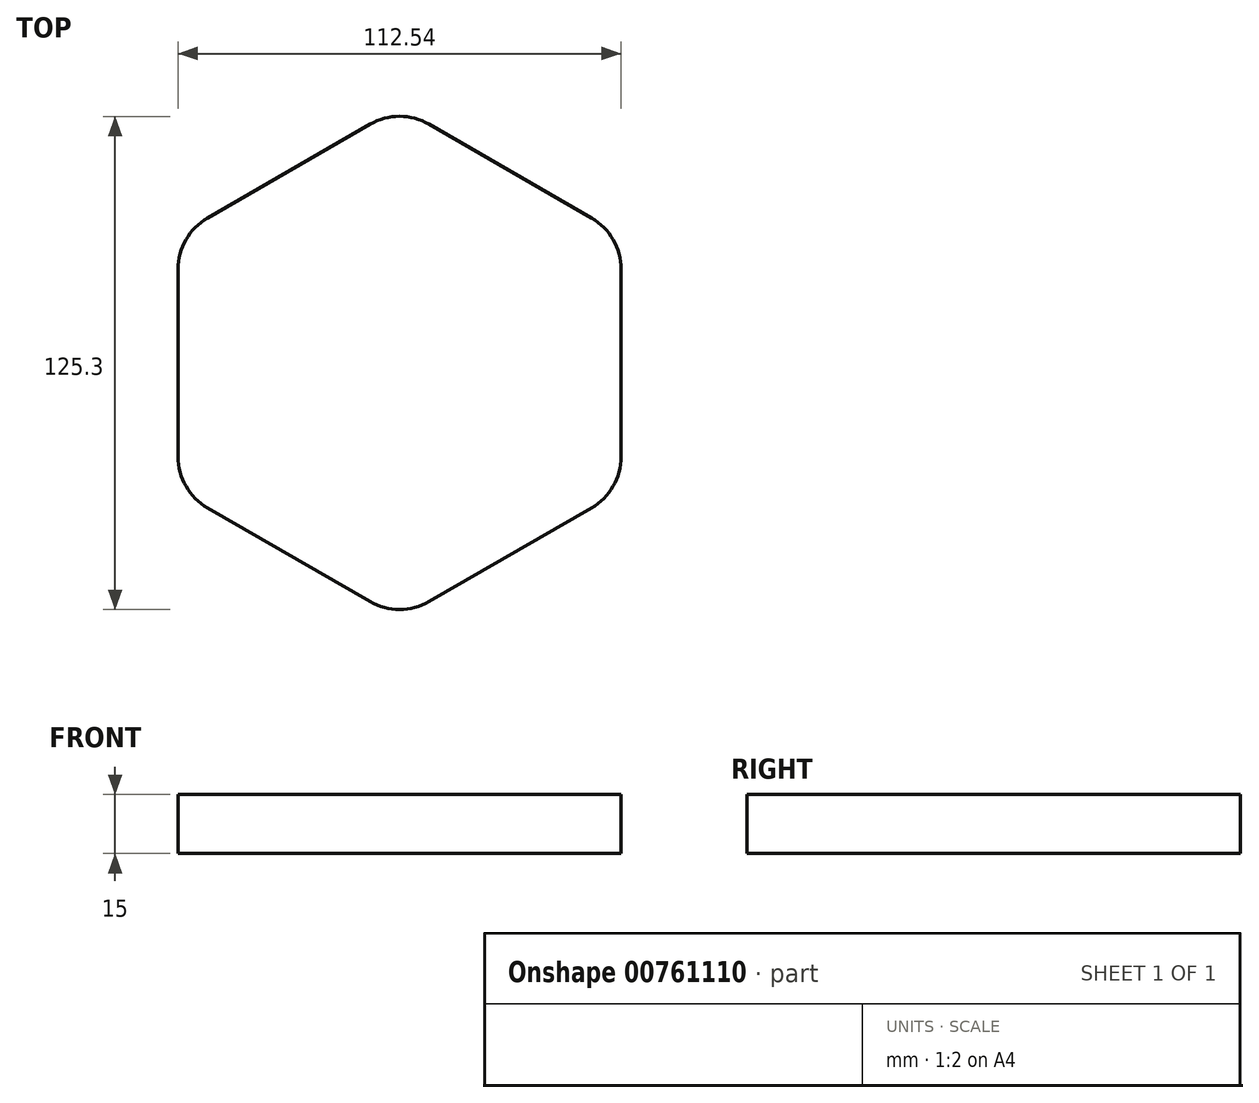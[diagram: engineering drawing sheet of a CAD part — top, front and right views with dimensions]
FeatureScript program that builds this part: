
annotation { "Feature Type Name" : "Feature", "Feature Type Description" : "" }
export const myFeature = defineFeature(function(context is Context, id is Id, definition is map)
    precondition{}
    {
        {
            var Q0;
            Q0=qCreatedBy(makeId("Top.planeOp"),FACE);
            var sketch = newSketch(context, id + "F0", { "sketchPlane" : qUnion([Q0])});
            skCircle(sketch, "E0.cCircle", {"center": v(0, 0) * mm, "radius": 64.98 * mm, "construction": true});
            skLineSegment(sketch, "E0.0", {"start": v(-7.5, -60.65) * mm, "end": v(-48.77, -36.82) * mm});
            skLineSegment(sketch, "E0.1", {"start": v(-56.27, -23.83) * mm, "end": v(-56.27, 23.83) * mm});
            skLineSegment(sketch, "E0.2", {"start": v(-48.77, 36.82) * mm, "end": v(-7.5, 60.65) * mm});
            skLineSegment(sketch, "E0.3", {"start": v(7.5, 60.65) * mm, "end": v(48.77, 36.82) * mm});
            skLineSegment(sketch, "E0.4", {"start": v(56.27, 23.83) * mm, "end": v(56.27, -23.83) * mm});
            skLineSegment(sketch, "E0.5", {"start": v(48.77, -36.82) * mm, "end": v(7.5, -60.65) * mm});
            skPoint(sketch, "E1.visualSharp", {"position": v(56.27, 32.49) * mm});
            skArc(sketch, "E1.filletArc", {"start": v(56.27, 23.83) * mm, "mid": v(54.26, 31.33) * mm, "end": v(48.77, 36.82) * mm});
            skPoint(sketch, "E2.visualSharp", {"position": v(56.27, -32.49) * mm});
            skArc(sketch, "E2.filletArc", {"start": v(48.77, -36.82) * mm, "mid": v(54.26, -31.33) * mm, "end": v(56.27, -23.83) * mm});
            skPoint(sketch, "E3.visualSharp", {"position": v(0, 64.98) * mm});
            skArc(sketch, "E3.filletArc", {"start": v(7.5, 60.65) * mm, "mid": v(0, 62.65) * mm, "end": v(-7.5, 60.65) * mm});
            skPoint(sketch, "E4.visualSharp", {"position": v(-56.27, 32.49) * mm});
            skArc(sketch, "E4.filletArc", {"start": v(-48.77, 36.82) * mm, "mid": v(-54.26, 31.33) * mm, "end": v(-56.27, 23.83) * mm});
            skPoint(sketch, "E5.visualSharp", {"position": v(-56.27, -32.49) * mm});
            skArc(sketch, "E5.filletArc", {"start": v(-56.27, -23.83) * mm, "mid": v(-54.26, -31.33) * mm, "end": v(-48.77, -36.82) * mm});
            skPoint(sketch, "E6.visualSharp", {"position": v(0, -64.98) * mm});
            skArc(sketch, "E6.filletArc", {"start": v(-7.5, -60.65) * mm, "mid": v(0, -62.65) * mm, "end": v(7.5, -60.65) * mm});
            skSolve(sketch);
        }
        {
            var Q0;
            Q0=makeQuery(id+"F0.imprint","IMPRINT",FACE,{"disambiguationData":[TD([[makeQuery(id+"F0.imprint","IMPRINT",EDGE,{"derivedFrom":sQuery(id+"F0.wireOp",EDGE,"E0.0")}),-1.0]])]});
            var Q1;
            Q1 = qSketchRegion(id + "F0", true);
            extrude(context, id + "F1", {"entities" : qUnion([Q0, Q1]), "endBound" : BoundingType.SYMMETRIC, "depth" : 15 * mm, "offsetDistance" : 25 * mm});
        }
    });
